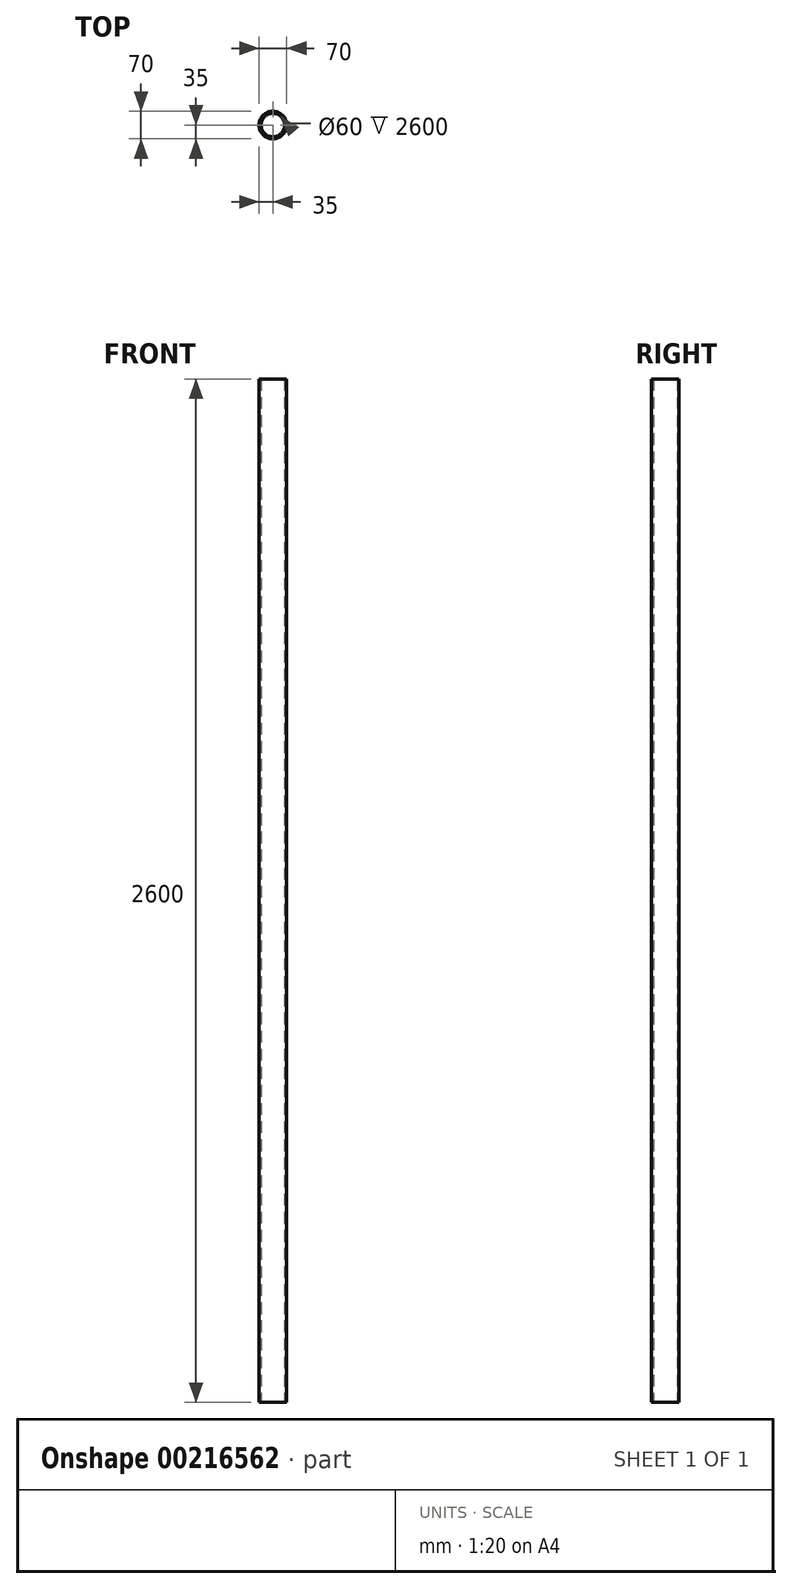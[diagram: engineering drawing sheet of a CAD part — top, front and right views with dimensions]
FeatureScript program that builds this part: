
annotation { "Feature Type Name" : "Feature", "Feature Type Description" : "" }
export const myFeature = defineFeature(function(context is Context, id is Id, definition is map)
    precondition{}
    {
        {
            var Q0;
            Q0=qCreatedBy(makeId("Top.planeOp"),FACE);
            var sketch = newSketch(context, id + "F0", { "sketchPlane" : qUnion([Q0])});
            skCircle(sketch, "E0", {"center": v(0, 0) * mm, "radius": 35 * mm});
            skCircle(sketch, "E1", {"center": v(0, 0) * mm, "radius": 30 * mm});
            skSolve(sketch);
        }
        {
            var Q0;
            Q0 = qSketchRegion(id + "F0", true);
            extrude(context, id + "F1", {"entities" : qUnion([Q0]), "depth" : 2200 * mm, "hasSecondDirection" : true, "secondDirectionOppositeDirection" : true, "secondDirectionDepth" : 400 * mm});
        }
    });
